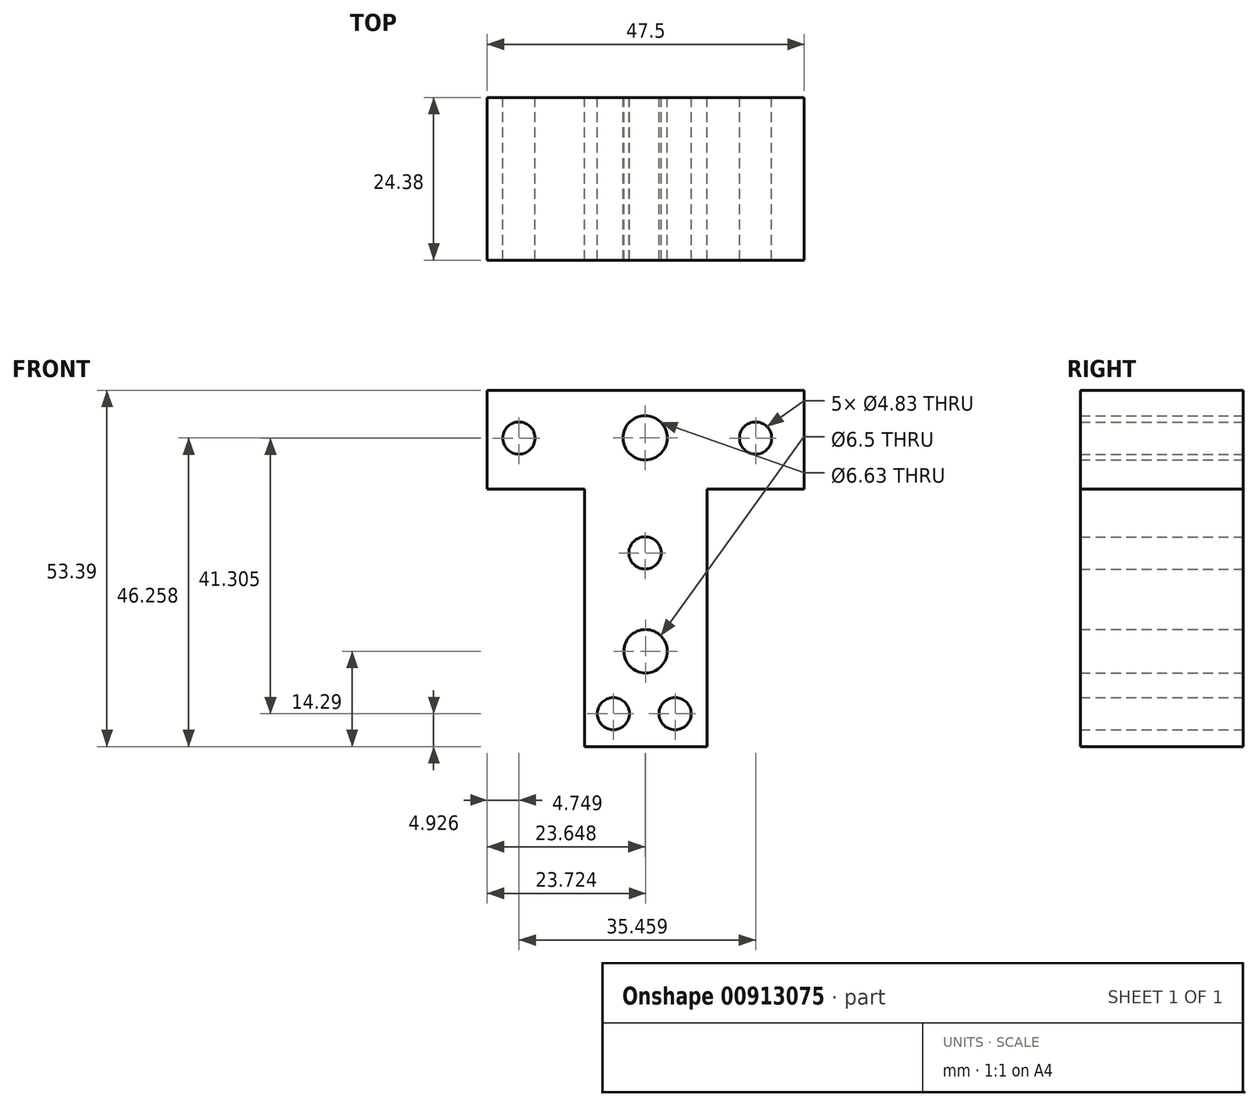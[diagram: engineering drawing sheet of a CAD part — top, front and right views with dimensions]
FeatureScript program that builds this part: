
annotation { "Feature Type Name" : "Feature", "Feature Type Description" : "" }
export const myFeature = defineFeature(function(context is Context, id is Id, definition is map)
    precondition{}
    {
        {
            var Q0;
            Q0=qCreatedBy(makeId("Front.planeOp"),FACE);
            var sketch = newSketch(context, id + "F0", { "sketchPlane" : qUnion([Q0])});
            skLineSegment(sketch, "E0", {"start": v(-14.58, 28.94) * mm, "end": v(32.92, 28.94) * mm});
            skLineSegment(sketch, "E1", {"start": v(32.92, 28.94) * mm, "end": v(32.92, 14.16) * mm});
            skLineSegment(sketch, "E2", {"start": v(-14.58, 28.94) * mm, "end": v(-14.58, 14.16) * mm});
            skLineSegment(sketch, "E3", {"start": v(-14.58, 14.16) * mm, "end": v(0, 14.16) * mm});
            skLineSegment(sketch, "E4", {"start": v(32.92, 14.16) * mm, "end": v(18.34, 14.16) * mm});
            skLineSegment(sketch, "E5", {"start": v(0, 14.16) * mm, "end": v(0, -24.45) * mm});
            skLineSegment(sketch, "E6", {"start": v(18.34, 14.16) * mm, "end": v(18.34, -24.45) * mm});
            skLineSegment(sketch, "E7", {"start": v(0, -24.45) * mm, "end": v(18.34, -24.45) * mm});
            skCircle(sketch, "E8", {"center": v(9.07, 21.8) * mm, "radius": 3.31 * mm});
            skCircle(sketch, "E9", {"center": v(9.14, -10.16) * mm, "radius": 3.25 * mm});
            skCircle(sketch, "E10", {"center": v(-9.83, 21.78) * mm, "radius": 2.41 * mm});
            skCircle(sketch, "E11", {"center": v(25.63, 21.78) * mm, "radius": 2.41 * mm});
            skPoint(sketch, "E12", {"position": v(25.63, 14.16) * mm});
            skCircle(sketch, "E13", {"center": v(9.07, 4.57) * mm, "radius": 2.41 * mm});
            skCircle(sketch, "E14", {"center": v(4.32, -19.52) * mm, "radius": 2.41 * mm});
            skCircle(sketch, "E15", {"center": v(13.57, -19.52) * mm, "radius": 2.41 * mm});
            skSolve(sketch);
        }
        {
            var Q0;
            Q0=makeQuery(id+"F0.imprint","IMPRINT",FACE,{"disambiguationData":[TD([[makeQuery(id+"F0.imprint","IMPRINT",EDGE,{"derivedFrom":sQuery(id+"F0.wireOp",EDGE,"E0")}),-1.0]])]});
            extrude(context, id + "F1", {"entities" : qUnion([Q0]), "depth" : 24.38 * mm, "offsetDistance" : 25.4 * mm});
        }
    });
